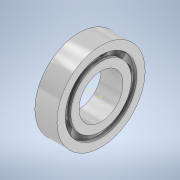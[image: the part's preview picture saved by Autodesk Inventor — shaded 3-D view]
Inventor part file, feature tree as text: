
AUTODESK INVENTOR PART (.ipt)
format: ipt  version: 2020.3 (Build 243373000, 373)  size: 280,064 bytes
history: native  units: mm
features: sketch x11, revolve x2, pattern_circular x1, projected_geometry x1
ambient origin geometry x8: Origin, YZ Plane, XZ Plane, XY Plane, X Axis, Y Axis, Z Axis, Center Point
bodies: Solid1 (feature_tree)
feature tree (15):
  sketch  "Sketch1"  dims[d6=8.0mm d7=3.0mm]
  sketch  "Sketch2"  dims[d8=8.0mm d9=3.0mm]
  revolve  "Revolution1"  [1 undecoded]
  sketch  "Sketch5"  dims[d10=2.0mm d11=8.0mm]
  sketch  "Sketch6"  dims[d12=6.0mm d13=1.0mm]
  sketch  "Sketch7"  dims[d15=90.0deg]
  revolve  "Revolution2"  [1 undecoded]
  pattern_circular  "Circular Pattern1"  Count=10 Angle=360.0deg
  sketch  "Sketch9"  dims[d17=90.0deg d18=100.0mm d19=360.0deg]
  sketch  "Sketch10"  dims[d30=32.0mm]
  sketch  "Sketch14"  dims[d31=26.0mm]
  sketch  "Sketch15"
  sketch  "Sketch16"
  sketch  "Sketch8"  dims[d16=4.6mm]
  projected_geometry  "Projected Loop1"
note: 2 required parameter values undecoded (feature->parameter linkage not recoverable at this tier; creation-order binding heuristic only, values carry confidence <= 0.55)
